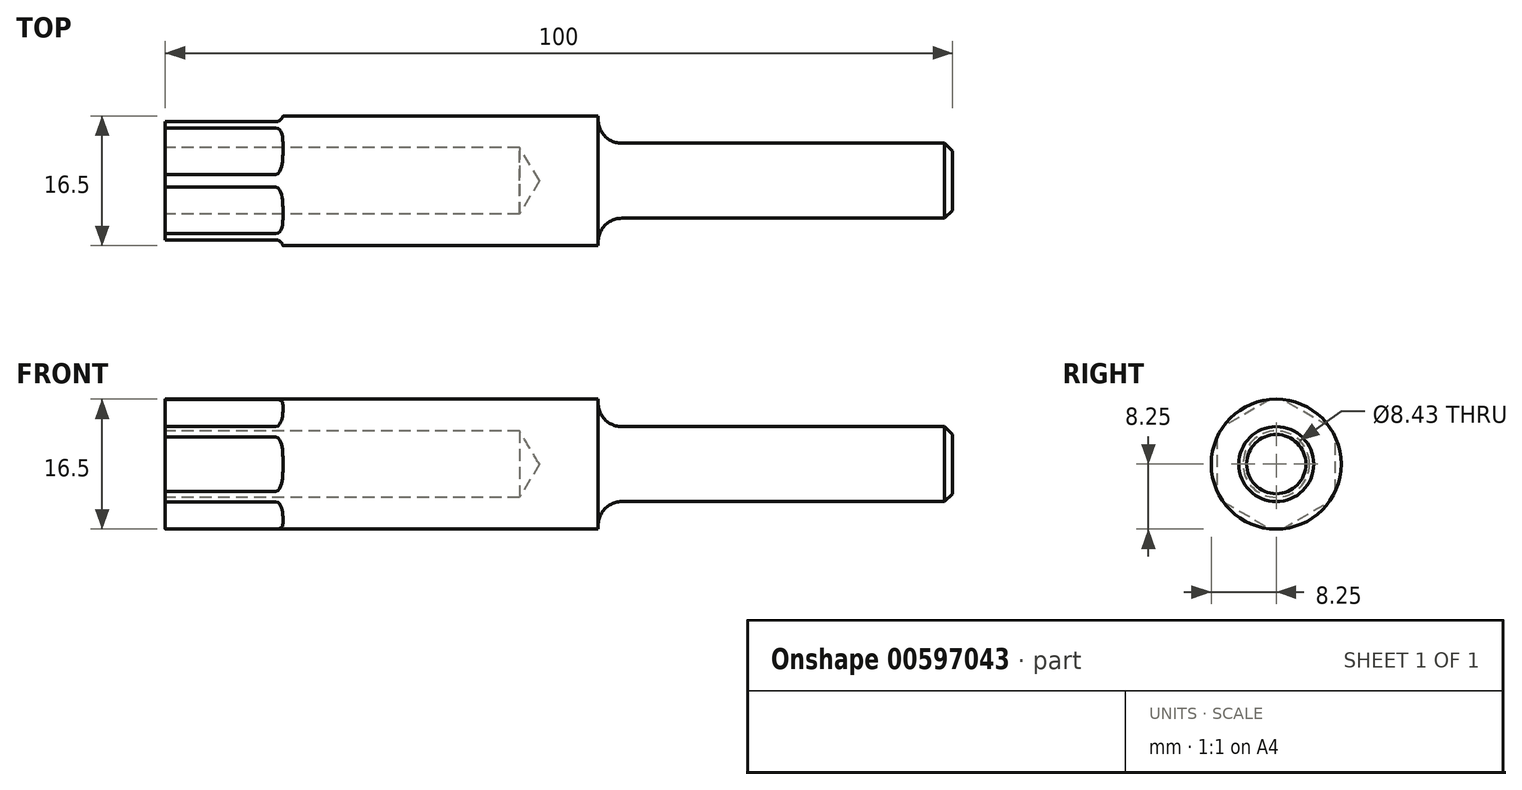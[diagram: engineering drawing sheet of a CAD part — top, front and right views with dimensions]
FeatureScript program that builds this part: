
annotation { "Feature Type Name" : "Feature", "Feature Type Description" : "" }
export const myFeature = defineFeature(function(context is Context, id is Id, definition is map)
    precondition{}
    {
        {
            var Q0;
            Q0=qCreatedBy(makeId("Front.planeOp"),FACE);
            var sketch = newSketch(context, id + "F0", { "sketchPlane" : qUnion([Q0])});
            skLineSegment(sketch, "E0", {"start": v(30, 0) * mm, "end": v(30, 8.25) * mm});
            skLineSegment(sketch, "E1", {"start": v(30, 8.25) * mm, "end": v(85, 8.25) * mm});
            skLineSegment(sketch, "E2", {"start": v(85, 8.25) * mm, "end": v(85, 4.76) * mm});
            skLineSegment(sketch, "E3", {"start": v(85, 4.76) * mm, "end": v(130, 4.76) * mm});
            skLineSegment(sketch, "E4", {"start": v(130, 4.76) * mm, "end": v(130, 0) * mm});
            skLineSegment(sketch, "E5", {"start": v(130, 0) * mm, "end": v(30, 0) * mm});
            skSolve(sketch);
        }
        {
            var Q0;
            Q0=makeQuery(id+"F0.imprint","IMPRINT",FACE,{"disambiguationData":[TD([[makeQuery(id+"F0.imprint","IMPRINT",EDGE,{"derivedFrom":sQuery(id+"F0.wireOp",EDGE,"E0")}),-1.0]])]});
            var Q1;
            Q1=sQuery(id+"F0.wireOp",EDGE,"E5");
            revolve(context, id + "F1", {"entities" : qUnion([Q0]), "axis" : qUnion([Q1]), "revolveType" : RevolveType.FULL});
        }
        {
            var Q0;
            Q0=makeQuery(id+"F1.opRevolve","SWEPT_FACE",FACE,{"disambiguationData":[OSD([sQuery(id+"F0.wireOp",EDGE,"E0")])]});
            var sketch = newSketch(context, id + "F2", { "sketchPlane" : qUnion([Q0])});
            skCircle(sketch, "E6.cCircle", {"center": v(0, 0) * mm, "radius": 7.5 * mm, "construction": true});
            skLineSegment(sketch, "E6.0", {"start": v(7.5, 4.33) * mm, "end": v(7.5, -4.33) * mm});
            skLineSegment(sketch, "E6.1", {"start": v(7.5, -4.33) * mm, "end": v(0, -8.66) * mm});
            skLineSegment(sketch, "E6.2", {"start": v(0, -8.66) * mm, "end": v(-7.5, -4.33) * mm});
            skLineSegment(sketch, "E6.3", {"start": v(-7.5, -4.33) * mm, "end": v(-7.5, 4.33) * mm});
            skLineSegment(sketch, "E6.4", {"start": v(-7.5, 4.33) * mm, "end": v(0, 8.66) * mm});
            skLineSegment(sketch, "E6.5", {"start": v(0, 8.66) * mm, "end": v(7.5, 4.33) * mm});
            skPoint(sketch, "E6.0.midPoint", {"position": v(7.5, 0) * mm});
            skCircle(sketch, "E7", {"center": v(0, 0) * mm, "radius": 25 * mm});
            skSolve(sketch);
        }
        {
            var Q0;
            Q0=sQuery(id+"F2.wireOp",VERTEX,"E6.cCircle.center");
            var Q1;
            Q1=makeQuery(id+"F1.opRevolve","SWEPT_BODY",BODY,{"disambiguationData":[OSD([sQuery(id+"F0.wireOp",EDGE,"E0"),sQuery(id+"F0.wireOp",EDGE,"E1"),sQuery(id+"F0.wireOp",EDGE,"E2"),sQuery(id+"F0.wireOp",EDGE,"E3"),sQuery(id+"F0.wireOp",EDGE,"E4"),sQuery(id+"F0.wireOp",EDGE,"E5")])]});
            hole(context, id + "F3", {"style" : HoleStyle.SIMPLE, "endStyle" : HoleEndStyle.BLIND, "standardTappedOrClearance" : lookupTablePath({ "standard" : "ANSI", "engagement" : "75%", "pitch" : "24 tpi", "size" : "3/8", "type" : "Tapped" }), "standardBlindInLast" : lookupTablePath({ "standard" : "ANSI", "engagement" : "75%", "pitch" : "24 tpi", "size" : "3/8", "type" : "Tapped" }), "holeDiameter" : 8.43 * mm, "majorDiameter" : 9.52 * mm, "showTappedDepth" : true, "holeDepth" : 45 * mm, "isTappedThrough" : true, "tappedDepth" : 42.88 * mm, "tapClearance" : 2, "startFromSketch" : true, "locations" : qUnion([Q0]), "scope" : qUnion([Q1])});
        }
        {
            var Q0;
            {var subQ0=sQuery(id+"F2.wireOp",EDGE,"E6.5");var subQ1=makeQuery(id+"F1.opRevolve","SWEPT_EDGE",EDGE,{"disambiguationData":[OSD([sQuery(id+"F0.wireOp",EDGE,"E0"),sQuery(id+"F0.wireOp",EDGE,"E1")])]});var subQ2=makeQuery(id+"F2.imprint","INTERSECT",VERTEX,{"disambiguationData":[OD(0.0)],"derivedFrom":[subQ1,subQ0]});Q0=makeQuery(id+"F2.imprint","IMPRINT",FACE,{"disambiguationData":[TD([[makeQuery(id+"F2.imprint","IMPRINT",EDGE,{"disambiguationData":[TD([[subQ2,-1.0]])],"derivedFrom":subQ0}),1.0]])]});}
            var Q1;
            {var subQ0=sQuery(id+"F2.wireOp",EDGE,"E6.4");var subQ1=makeQuery(id+"F1.opRevolve","SWEPT_EDGE",EDGE,{"disambiguationData":[OSD([sQuery(id+"F0.wireOp",EDGE,"E0"),sQuery(id+"F0.wireOp",EDGE,"E1")])]});var subQ2=makeQuery(id+"F2.imprint","INTERSECT",VERTEX,{"disambiguationData":[OD(0.0)],"derivedFrom":[subQ1,subQ0]});Q1=makeQuery(id+"F2.imprint","IMPRINT",FACE,{"disambiguationData":[TD([[makeQuery(id+"F2.imprint","IMPRINT",EDGE,{"disambiguationData":[TD([[subQ2,-1.0]])],"derivedFrom":subQ0}),1.0]])]});}
            var Q2;
            {var subQ0=sQuery(id+"F2.wireOp",EDGE,"E6.1");var subQ1=makeQuery(id+"F1.opRevolve","SWEPT_EDGE",EDGE,{"disambiguationData":[OSD([sQuery(id+"F0.wireOp",EDGE,"E0"),sQuery(id+"F0.wireOp",EDGE,"E1")])]});var subQ2=makeQuery(id+"F2.imprint","INTERSECT",VERTEX,{"disambiguationData":[OD(0.0)],"derivedFrom":[subQ1,subQ0]});Q2=makeQuery(id+"F2.imprint","IMPRINT",FACE,{"disambiguationData":[TD([[makeQuery(id+"F2.imprint","IMPRINT",EDGE,{"disambiguationData":[TD([[subQ2,-1.0]])],"derivedFrom":subQ0}),1.0]])]});}
            var Q3;
            {var subQ0=sQuery(id+"F2.wireOp",EDGE,"E6.0");var subQ1=makeQuery(id+"F1.opRevolve","SWEPT_EDGE",EDGE,{"disambiguationData":[OSD([sQuery(id+"F0.wireOp",EDGE,"E0"),sQuery(id+"F0.wireOp",EDGE,"E1")])]});var subQ2=makeQuery(id+"F2.imprint","INTERSECT",VERTEX,{"disambiguationData":[OD(0.0)],"derivedFrom":[subQ1,subQ0]});Q3=makeQuery(id+"F2.imprint","IMPRINT",FACE,{"disambiguationData":[TD([[makeQuery(id+"F2.imprint","IMPRINT",EDGE,{"disambiguationData":[TD([[subQ2,-1.0]])],"derivedFrom":subQ0}),1.0]])]});}
            var Q4;
            {var subQ0=sQuery(id+"F2.wireOp",EDGE,"E6.3");var subQ1=makeQuery(id+"F1.opRevolve","SWEPT_EDGE",EDGE,{"disambiguationData":[OSD([sQuery(id+"F0.wireOp",EDGE,"E0"),sQuery(id+"F0.wireOp",EDGE,"E1")])]});var subQ2=makeQuery(id+"F2.imprint","INTERSECT",VERTEX,{"disambiguationData":[OD(0.0)],"derivedFrom":[subQ1,subQ0]});Q4=makeQuery(id+"F2.imprint","IMPRINT",FACE,{"disambiguationData":[TD([[makeQuery(id+"F2.imprint","IMPRINT",EDGE,{"disambiguationData":[TD([[subQ2,-1.0]])],"derivedFrom":subQ0}),1.0]])]});}
            var Q5;
            {var subQ0=sQuery(id+"F2.wireOp",EDGE,"E6.2");var subQ1=makeQuery(id+"F1.opRevolve","SWEPT_EDGE",EDGE,{"disambiguationData":[OSD([sQuery(id+"F0.wireOp",EDGE,"E0"),sQuery(id+"F0.wireOp",EDGE,"E1")])]});var subQ2=makeQuery(id+"F2.imprint","INTERSECT",VERTEX,{"disambiguationData":[OD(0.0)],"derivedFrom":[subQ1,subQ0]});Q5=makeQuery(id+"F2.imprint","IMPRINT",FACE,{"disambiguationData":[TD([[makeQuery(id+"F2.imprint","IMPRINT",EDGE,{"disambiguationData":[TD([[subQ2,-1.0]])],"derivedFrom":subQ0}),1.0]])]});}
            extrude(context, id + "F4", {"entities" : qUnion([Q0, Q1, Q2, Q3, Q4, Q5]), "operationType" : NewBodyOperationType.REMOVE, "oppositeDirection" : true, "depth" : 15 * mm, "offsetDistance" : 25 * mm});
        }
        {
            var Q0;
            Q0=makeQuery(id+"F4.boolean.opBoolean","COPY",EDGE,{"derivedFrom":makeQuery(id+"F4.opExtrude","CAP_EDGE",EDGE,{"disambiguationData":[OSD([sQuery(id+"F2.wireOp",EDGE,"E6.5")])],"isStart":false})});
            var Q1;
            Q1=makeQuery(id+"F4.boolean.opBoolean","COPY",EDGE,{"derivedFrom":makeQuery(id+"F4.opExtrude","CAP_EDGE",EDGE,{"disambiguationData":[OSD([sQuery(id+"F2.wireOp",EDGE,"E6.0")])],"isStart":false})});
            var Q2;
            Q2=makeQuery(id+"F4.boolean.opBoolean","COPY",EDGE,{"derivedFrom":makeQuery(id+"F4.opExtrude","CAP_EDGE",EDGE,{"disambiguationData":[OSD([sQuery(id+"F2.wireOp",EDGE,"E6.4")])],"isStart":false})});
            var Q3;
            Q3=makeQuery(id+"F4.boolean.opBoolean","COPY",EDGE,{"derivedFrom":makeQuery(id+"F4.opExtrude","CAP_EDGE",EDGE,{"disambiguationData":[OSD([sQuery(id+"F2.wireOp",EDGE,"E6.3")])],"isStart":false})});
            var Q4;
            Q4=makeQuery(id+"F4.boolean.opBoolean","COPY",EDGE,{"derivedFrom":makeQuery(id+"F4.opExtrude","CAP_EDGE",EDGE,{"disambiguationData":[OSD([sQuery(id+"F2.wireOp",EDGE,"E6.2")])],"isStart":false})});
            var Q5;
            Q5=makeQuery(id+"F4.boolean.opBoolean","COPY",EDGE,{"derivedFrom":makeQuery(id+"F4.opExtrude","CAP_EDGE",EDGE,{"disambiguationData":[OSD([sQuery(id+"F2.wireOp",EDGE,"E6.1")])],"isStart":false})});
            fillet(context, id + "F5", {"entities" : qUnion([Q0, Q1, Q2, Q3, Q4, Q5]), "radius" : 1 * mm, "tangentPropagation" : true, "allowEdgeOverflow" : false});
        }
        {
            var Q0;
            Q0=makeQuery(id+"F1.opRevolve","SWEPT_EDGE",EDGE,{"disambiguationData":[OSD([sQuery(id+"F0.wireOp",EDGE,"E3"),sQuery(id+"F0.wireOp",EDGE,"E4")])]});
            chamfer(context, id + "F6", {"entities" : qUnion([Q0]), "width" : 1 * mm, "tangentPropagation" : true});
        }
        {
            var Q0;
            Q0=makeQuery(id+"F1.opRevolve","SWEPT_EDGE",EDGE,{"disambiguationData":[OSD([sQuery(id+"F0.wireOp",EDGE,"E2"),sQuery(id+"F0.wireOp",EDGE,"E3")])]});
            fillet(context, id + "F7", {"entities" : qUnion([Q0]), "radius" : 3 * mm, "tangentPropagation" : true, "allowEdgeOverflow" : false});
        }
    });
